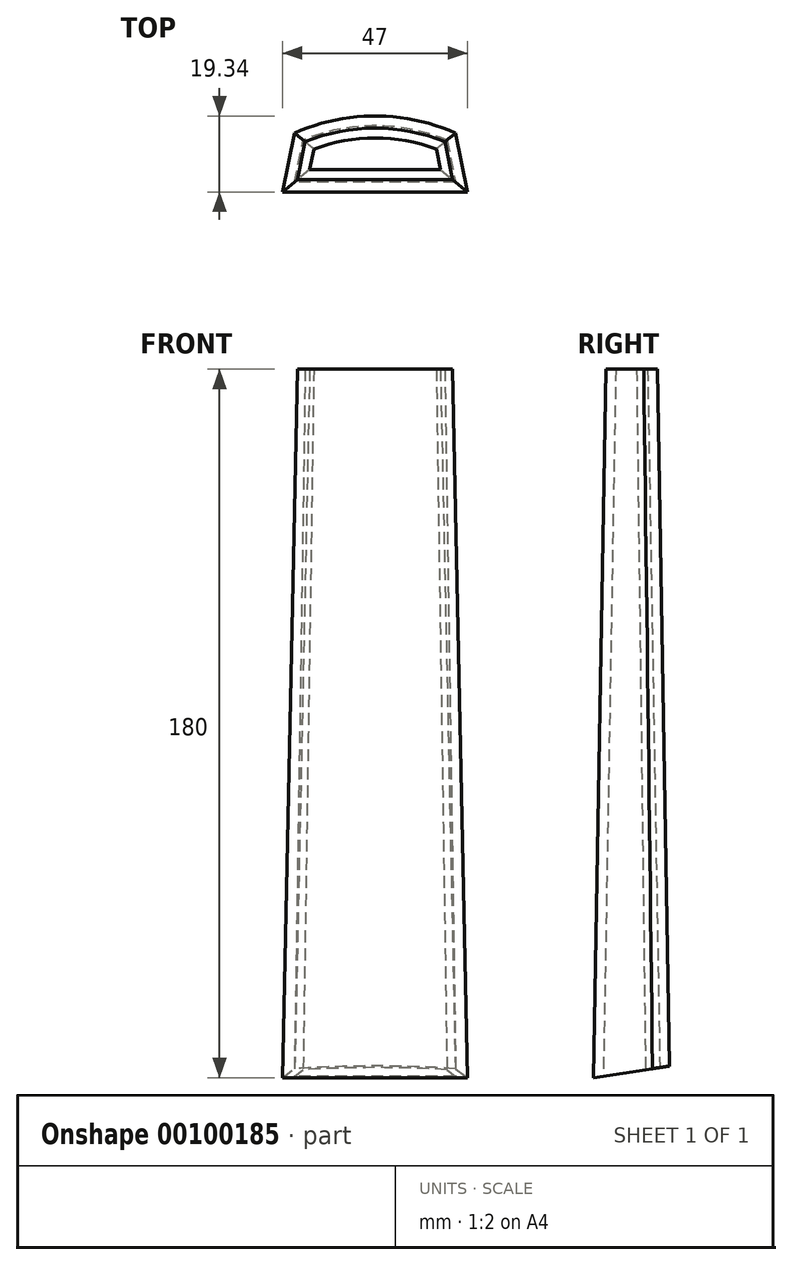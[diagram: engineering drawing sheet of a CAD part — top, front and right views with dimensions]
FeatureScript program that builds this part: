
annotation { "Feature Type Name" : "Feature", "Feature Type Description" : "" }
export const myFeature = defineFeature(function(context is Context, id is Id, definition is map)
    precondition{}
    {
        {
            var Q0;
            Q0=qCreatedBy(makeId("Top.planeOp"),FACE);
            var sketch = newSketch(context, id + "F3", { "sketchPlane" : qUnion([Q0])});
            skLineSegment(sketch, "E0", {"start": v(0, 0) * mm, "end": v(47, 0) * mm});
            skLineSegment(sketch, "E1", {"start": v(47, 0) * mm, "end": v(44, 15) * mm});
            skArc(sketch, "E2", {"start": v(44, 15) * mm, "mid": v(23.5, 19.4) * mm, "end": v(3, 15) * mm});
            skLineSegment(sketch, "E3", {"start": v(3, 15) * mm, "end": v(0, 0) * mm});
            skSolve(sketch);
        }
        {
            var Q0;
            Q0=makeQuery(id+"F3.imprint","IMPRINT",FACE,{"disambiguationData":[TD([[makeQuery(id+"F3.imprint","IMPRINT",EDGE,{"derivedFrom":sQuery(id+"F3.wireOp",EDGE,"E0")}),1.0]])]});
            extrude(context, id + "F0", {"entities" : qUnion([Q0]), "depth" : 180 * mm, "hasDraft" : true, "draftAngle" : 1 * degree, "draftPullDirection" : true});
        }
        {
            var Q0;
            Q0=qCreatedBy(makeId("Right.planeOp"),FACE);
            var sketch = newSketch(context, id + "F1", { "sketchPlane" : qUnion([Q0])});
            skLineSegment(sketch, "E4", {"start": v(0, 0) * mm, "end": v(25.97, 3.93) * mm});
            skLineSegment(sketch, "E5", {"start": v(25.97, 3.93) * mm, "end": v(25.97, 3.93) * mm});
            skLineSegment(sketch, "E6", {"start": v(25.97, 3.93) * mm, "end": v(27.55, -6.5) * mm});
            skLineSegment(sketch, "E7", {"start": v(27.55, -6.5) * mm, "end": v(27.46, -6.74) * mm});
            skLineSegment(sketch, "E8", {"start": v(27.46, -6.74) * mm, "end": v(-2.05, -6.74) * mm});
            skLineSegment(sketch, "E9", {"start": v(-2.05, -6.74) * mm, "end": v(0, 0) * mm});
            skSolve(sketch);
        }
        {
            var Q0;
            Q0=makeQuery(id+"F1.imprint","IMPRINT",FACE,{"disambiguationData":[TD([[makeQuery(id+"F1.imprint","IMPRINT",EDGE,{"derivedFrom":sQuery(id+"F1.wireOp",EDGE,"E4")}),-1.0]])]});
            extrude(context, id + "F2", {"entities" : qUnion([Q0]), "operationType" : NewBodyOperationType.REMOVE, "depth" : 100 * mm});
        }
        {
            var Q0;
            Q0=makeQuery(id+"F2.boolean.opBoolean","COPY",FACE,{"derivedFrom":makeQuery(id+"F2.opExtrude","SWEPT_FACE",FACE,{"disambiguationData":[OSD([sQuery(id+"F1.wireOp",EDGE,"E4")])]})});
            var Q1;
            Q1=makeQuery(id+"F0.opExtrude","CAP_FACE",FACE,{"disambiguationData":[OSD([sQuery(id+"F3.wireOp",EDGE,"E0"),sQuery(id+"F3.wireOp",EDGE,"E1"),sQuery(id+"F3.wireOp",EDGE,"E2"),sQuery(id+"F3.wireOp",EDGE,"E3")])],"isStart":false});
            shell(context, id + "F4", {"entities" : qUnion([Q0, Q1]), "thickness" : 2.5 * mm});
        }
    });
